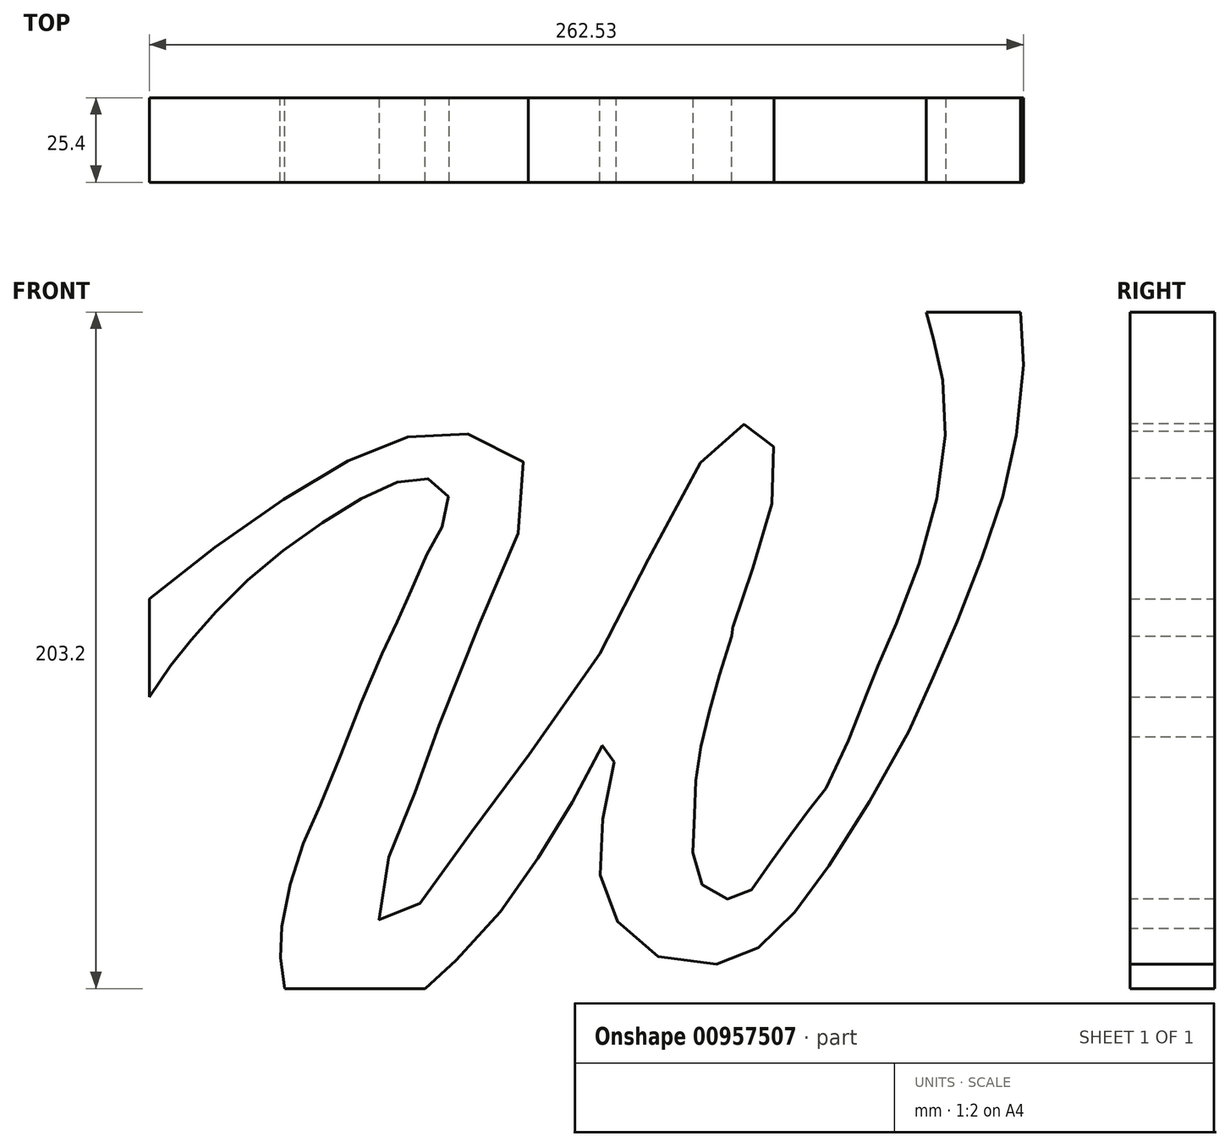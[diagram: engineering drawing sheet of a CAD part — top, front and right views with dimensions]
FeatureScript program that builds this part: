
annotation { "Feature Type Name" : "Feature", "Feature Type Description" : "" }
export const myFeature = defineFeature(function(context is Context, id is Id, definition is map)
    precondition{}
    {
        {
            var Q0;
            Q0=qCreatedBy(makeId("Front.planeOp"),FACE);
            var sketch = newSketch(context, id + "F0", { "sketchPlane" : qUnion([Q0])});
            skLineSegment(sketch, "E0", {"start": v(-144.58, 106.22) * mm, "end": v(164.13, 106.22) * mm});
            skLineSegment(sketch, "E1", {"start": v(164.13, -96.98) * mm, "end": v(-144.58, -96.98) * mm});
            skLineSegment(sketch, "E2", {"start": v(-144.58, 106.22) * mm, "end": v(-144.58, -96.98) * mm});
            skFitSpline(sketch, "E3", {"points": [v(-144.58, 20.04) * mm, v(-131.13, 30.74) * mm, v(-113.55, 43.73) * mm, v(-100.94, 52.14) * mm, v(-87.57, 60.17) * mm, v(-77.72, 64.94) * mm, v(-66.82, 68.8) * mm, v(-54.55, 70.39) * mm, v(-48.19, 69.48) * mm, v(-37.6, 65.92) * mm, v(-31.12, 58.35) * mm, v(-32.74, 42.68) * mm, v(-37.88, 30.52) * mm, v(-53.28, -7.3) * mm, v(-59.5, -23.25) * mm, v(-64.09, -36.49) * mm, v(-69.1, -47.34) * mm, v(-73.42, -60.58) * mm, v(-75.3, -71.4) * mm, v(-74.77, -78.15) * mm, v(-69.63, -78.15) * mm, v(-60.45, -67.34) * mm, v(-48.02, -50.32) * mm, v(-34.78, -32.48) * mm, v(-11.54, 0) * mm, v(2.51, 25.88) * mm, v(17.91, 56.68) * mm, v(28.18, 68.84) * mm, v(32.77, 72.09) * mm, v(37.37, 72.36) * mm, v(40.6, 69.65) * mm, v(42.77, 66.14) * mm, v(42.77, 59.66) * mm, v(42.5, 49.66) * mm, v(39.26, 38.31) * mm, v(35.75, 26.7) * mm, v(31.7, 16.42) * mm, v(30.34, 8.86) * mm], "startDerivative": vector(414.85, 335.76) * mm, "endDerivative": vector(-39.33, -359.1) * mm});
            skFitSpline(sketch, "E4", {"points": [v(30.34, 8.86) * mm, v(25.2, -7.8) * mm, v(21.57, -22.11) * mm, v(19.53, -34.6) * mm, v(19.07, -47.56) * mm, v(19.53, -62.33) * mm, v(26.34, -69.37) * mm, v(34.07, -69.14) * mm, v(40.2, -61.87) * mm, v(47.93, -50.97) * mm, v(53.6, -43.24) * mm, v(59.3, -35.74) * mm, v(71.33, -7.34) * mm, v(74.29, 0) * mm, v(86.33, 29.92) * mm, v(94.64, 74.4) * mm, v(91, 98.02) * mm, v(88.73, 106.22) * mm], "startDerivative": vector(-85.73, -268.86) * mm, "endDerivative": vector(-47.31, 165.37) * mm});
            skFitSpline(sketch, "E5", {"points": [v(30.34, 8.86) * mm, v(25.2, -7.8) * mm, v(21.57, -22.11) * mm, v(19.53, -34.6) * mm, v(19.07, -47.56) * mm, v(19.53, -62.33) * mm, v(26.34, -69.37) * mm, v(34.07, -69.14) * mm, v(40.2, -61.87) * mm, v(47.93, -50.97) * mm, v(53.6, -43.24) * mm, v(59.3, -35.74) * mm, v(71.33, -7.34) * mm, v(74.29, 0) * mm, v(86.33, 29.92) * mm, v(94.64, 74.4) * mm, v(91, 98.02) * mm, v(88.73, 106.22) * mm], "startDerivative": vector(-85.73, -268.86) * mm, "endDerivative": vector(-47.31, 165.37) * mm});
            skLineSegment(sketch, "E6", {"start": v(30.68, 11.68) * mm, "end": v(30.34, 8.86) * mm});
            skFitSpline(sketch, "E7", {"points": [v(-144.58, -9.37) * mm, v(-136.78, 1.96) * mm, v(-129.67, 10.4) * mm, v(-117.68, 23.28) * mm, v(-101.02, 37.05) * mm, v(-82.37, 49.26) * mm, v(-68.38, 55.7) * mm, v(-59.5, 55.7) * mm, v(-54.6, 50.15) * mm, v(-57.27, 40.38) * mm, v(-62.16, 31.5) * mm, v(-68.15, 17.28) * mm, v(-72.37, 8.62) * mm, v(-82.37, -14.7) * mm, v(-93.47, -42.46) * mm, v(-100.13, -58.23) * mm, v(-104.58, -77.32) * mm, v(-105.24, -87.54) * mm, v(-103.9, -96.98) * mm], "startDerivative": vector(146.97, 223.06) * mm, "endDerivative": vector(38.6, -213.86) * mm});
            skFitSpline(sketch, "E8", {"points": [v(-61.8, -96.98) * mm, v(-58.43, -94.54) * mm, v(-53.76, -89.87) * mm, v(-48.9, -85.2) * mm, v(-37.51, -71.95) * mm, v(-30.6, -61.86) * mm, v(-22.2, -49.16) * mm, v(-16.6, -39.08) * mm, v(-10.43, -27.5) * mm, v(-5.95, -21.34) * mm, v(-4.46, -23.02) * mm, v(-5.4, -30.3) * mm, v(-7.82, -40.2) * mm, v(-8.75, -51.78) * mm, v(-9.31, -60.74) * mm, v(-7.63, -69.14) * mm, v(-4.65, -75.68) * mm, v(0, -82.59) * mm, v(8.8, -87.54) * mm, v(19.82, -89.5) * mm, v(28.97, -89.31) * mm, v(34.07, -87.54) * mm, v(40.17, -83.15) * mm, v(45.96, -77.36) * mm, v(51.2, -71.95) * mm, v(56.05, -65.4) * mm, v(67.91, -47.24) * mm, v(73.99, -36.68) * mm, v(84.82, -17.14) * mm, v(89.04, -7.1) * mm, v(92.74, 0) * mm, v(97.5, 11.65) * mm, v(101.96, 23.9) * mm, v(107.96, 38.56) * mm, v(111.73, 50.55) * mm, v(114.17, 61.43) * mm, v(116.84, 75.87) * mm, v(117.95, 91.41) * mm, v(117.5, 103.63) * mm, v(117.06, 106.22) * mm], "startDerivative": vector(198.07, 127.05) * mm, "endDerivative": vector(-35.44, 159.92) * mm});
            skLineSegment(sketch, "E9", {"start": v(164.13, 106.22) * mm, "end": v(164.13, -96.98) * mm});
            skSolve(sketch);
        }
        {
            var Q0;
            {var subQ0=sQuery(id+"F0.wireOp",EDGE,"E3");Q0=makeQuery(id+"F0.imprint","IMPRINT",FACE,{"disambiguationData":[TD([[makeQuery(id+"F0.imprint","IMPRINT",EDGE,{"derivedFrom":subQ0}),-1.0]])]});}
            extrude(context, id + "F1", {"entities" : qUnion([Q0]), "depth" : 25.4 * mm, "offsetDistance" : 25.4 * mm});
        }
    });
